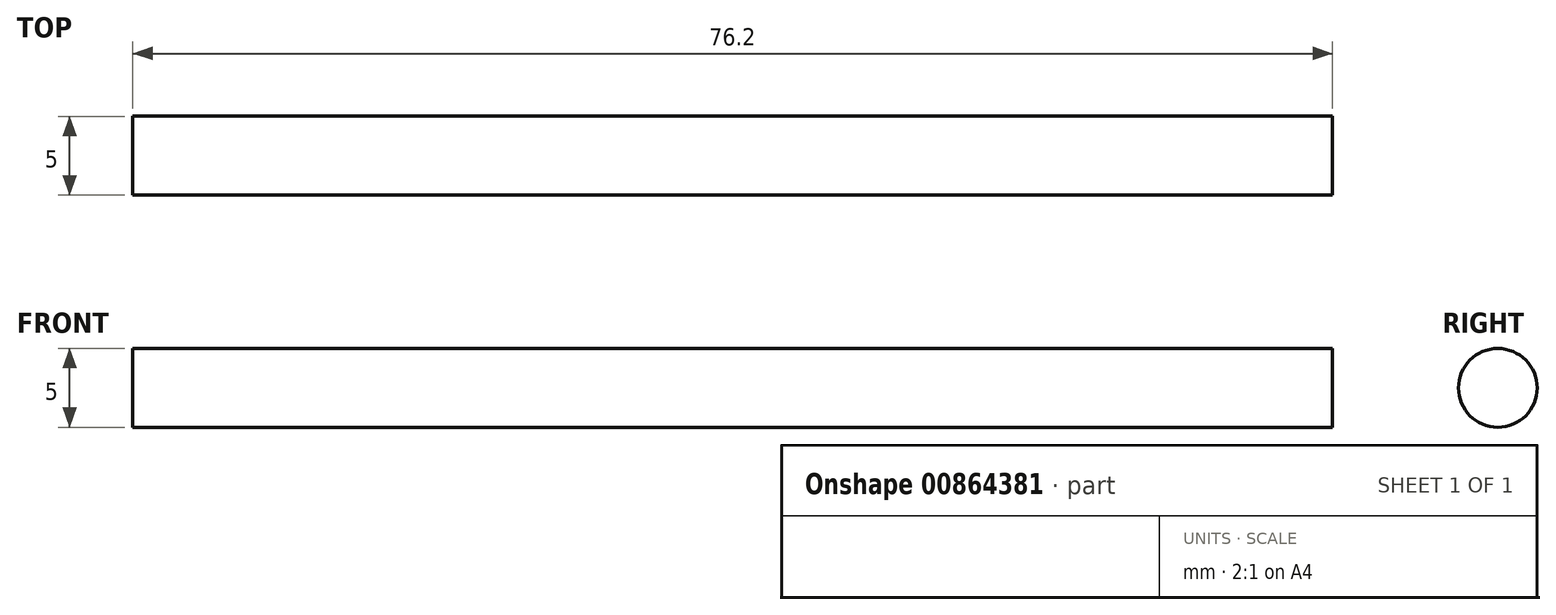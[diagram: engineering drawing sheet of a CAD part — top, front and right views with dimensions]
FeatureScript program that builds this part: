
annotation { "Feature Type Name" : "Feature", "Feature Type Description" : "" }
export const myFeature = defineFeature(function(context is Context, id is Id, definition is map)
    precondition{}
    {
        {
            var Q0;
            Q0=qCreatedBy(makeId("Front.planeOp"),FACE);
            var sketch = newSketch(context, id + "F0", { "sketchPlane" : qUnion([Q0])});
            skLineSegment(sketch, "E0", {"start": v(0, 0) * mm, "end": v(76.2, 0) * mm});
            skSolve(sketch);
        }
        {
            var Q0;
            Q0=qCreatedBy(makeId("Right.planeOp"),FACE);
            var sketch = newSketch(context, id + "F1", { "sketchPlane" : qUnion([Q0])});
            skCircle(sketch, "E1", {"center": v(0, 0) * mm, "radius": 2.5 * mm});
            skSolve(sketch);
        }
        {
            var Q0;
            Q0=makeQuery(id+"F1.imprint","IMPRINT",FACE,{"disambiguationData":[TD([[makeQuery(id+"F1.imprint","IMPRINT",EDGE,{"derivedFrom":sQuery(id+"F1.wireOp",EDGE,"E1")}),1.0]])]});
            var Q1;
            Q1=qConstructionFilter(qBodyType(qCreatedBy(id+"F0",EDGE),BodyType.WIRE),ConstructionObject.NO);
            sweep(context, id + "F2", {"profiles" : qUnion([Q0]), "path" : qUnion([Q1]), "keepProfileOrientation" : true});
        }
    });
